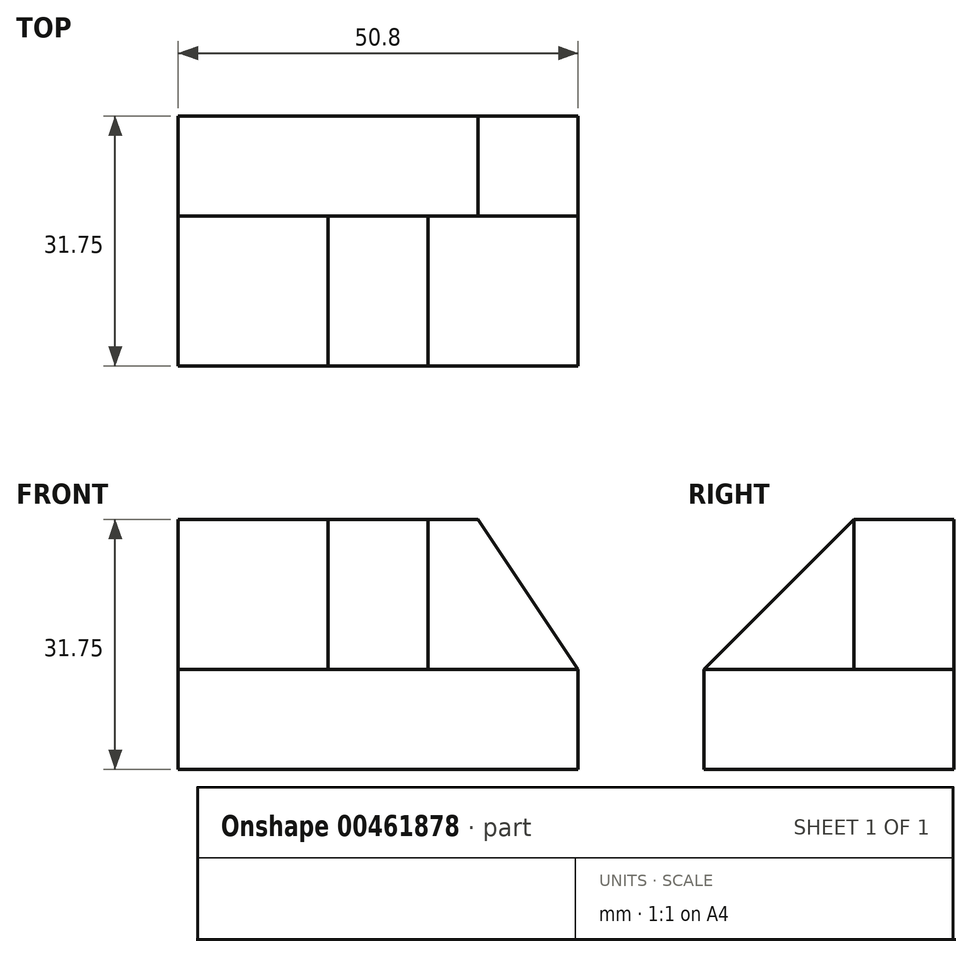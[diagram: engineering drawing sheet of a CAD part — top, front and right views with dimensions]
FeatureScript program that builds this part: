
annotation { "Feature Type Name" : "Feature", "Feature Type Description" : "" }
export const myFeature = defineFeature(function(context is Context, id is Id, definition is map)
    precondition{}
    {
        {
            var Q0;
            Q0=qCreatedBy(makeId("Right.planeOp"),FACE);
            var sketch = newSketch(context, id + "F0", { "sketchPlane" : qUnion([Q0])});
            skLineSegment(sketch, "E0.bottom", {"start": v(0, 0) * mm, "end": v(31.75, 0) * mm});
            skLineSegment(sketch, "E0.top", {"start": v(0, 31.75) * mm, "end": v(31.75, 31.75) * mm});
            skLineSegment(sketch, "E0.left", {"start": v(0, 0) * mm, "end": v(0, 31.75) * mm});
            skLineSegment(sketch, "E0.right", {"start": v(31.75, 0) * mm, "end": v(31.75, 31.75) * mm});
            skSolve(sketch);
        }
        {
            var Q0;
            Q0 = qSketchRegion(id + "F0", true);
            extrude(context, id + "F1", {"entities" : qUnion([Q0]), "depth" : 50.8 * mm});
        }
        {
            var Q0;
            Q0=makeQuery(id+"F1.opExtrude","CAP_FACE",FACE,{"disambiguationData":[OSD([sQuery(id+"F0.wireOp",EDGE,"E0.bottom"),sQuery(id+"F0.wireOp",EDGE,"E0.top"),sQuery(id+"F0.wireOp",EDGE,"E0.left"),sQuery(id+"F0.wireOp",EDGE,"E0.right")])],"isStart":false});
            var sketch = newSketch(context, id + "F2", { "sketchPlane" : qUnion([Q0])});
            skLineSegment(sketch, "E1", {"start": v(31.75, 31.75) * mm, "end": v(19.05, 31.75) * mm});
            skLineSegment(sketch, "E2", {"start": v(19.05, 31.75) * mm, "end": v(19.05, 12.7) * mm});
            skLineSegment(sketch, "E3", {"start": v(19.05, 12.7) * mm, "end": v(0, 12.7) * mm});
            skLineSegment(sketch, "E4", {"start": v(0, 12.7) * mm, "end": v(0, 0) * mm});
            skLineSegment(sketch, "E5", {"start": v(0, 12.7) * mm, "end": v(19.05, 31.75) * mm});
            skSolve(sketch);
        }
        {
            var Q0;
            {var subQ0=sQuery(id+"F2.wireOp",EDGE,"E5");Q0=makeQuery(id+"F2.imprint","IMPRINT",FACE,{"disambiguationData":[TD([[makeQuery(id+"F2.imprint","IMPRINT",EDGE,{"derivedFrom":subQ0}),1.0]])]});}
            extrude(context, id + "F3", {"entities" : qUnion([Q0]), "operationType" : NewBodyOperationType.REMOVE, "oppositeDirection" : true, "depth" : 50.8 * mm});
        }
        {
            var Q0;
            Q0=makeQuery(id+"F1.opExtrude","CAP_FACE",FACE,{"disambiguationData":[OSD([sQuery(id+"F0.wireOp",EDGE,"E0.bottom"),sQuery(id+"F0.wireOp",EDGE,"E0.top"),sQuery(id+"F0.wireOp",EDGE,"E0.left"),sQuery(id+"F0.wireOp",EDGE,"E0.right")])],"isStart":false});
            var sketch = newSketch(context, id + "F4", { "sketchPlane" : qUnion([Q0])});
            skLineSegment(sketch, "E6", {"start": v(19.05, 31.75) * mm, "end": v(0, 12.7) * mm});
            skLineSegment(sketch, "E7", {"start": v(0, 12.7) * mm, "end": v(19.05, 12.7) * mm});
            skLineSegment(sketch, "E8", {"start": v(19.05, 12.7) * mm, "end": v(19.05, 31.75) * mm});
            skSolve(sketch);
        }
        {
            var Q0;
            Q0=makeQuery(id+"F4.imprint","IMPRINT",FACE,{"disambiguationData":[TD([[makeQuery(id+"F4.imprint","IMPRINT",EDGE,{"derivedFrom":sQuery(id+"F4.wireOp",EDGE,"E6")}),-1.0]])]});
            extrude(context, id + "F5", {"entities" : qUnion([Q0]), "operationType" : NewBodyOperationType.REMOVE, "oppositeDirection" : true, "depth" : 19.05 * mm});
        }
        {
            var Q0;
            Q0=makeQuery(id+"F5.boolean.opBoolean","COPY",FACE,{"derivedFrom":makeQuery(id+"F5.opExtrude","SWEPT_FACE",FACE,{"disambiguationData":[OSD([sQuery(id+"F4.wireOp",EDGE,"E8")])]})});
            var sketch = newSketch(context, id + "F6", { "sketchPlane" : qUnion([Q0])});
            skLineSegment(sketch, "E9", {"start": v(50.8, 31.75) * mm, "end": v(38.07, 31.75) * mm});
            skLineSegment(sketch, "E10", {"start": v(38.07, 31.75) * mm, "end": v(50.8, 12.7) * mm});
            skSolve(sketch);
        }
        {
            var Q0;
            Q0=makeQuery(id+"F6.imprint","IMPRINT",FACE,{"disambiguationData":[TD([[makeQuery(id+"F6.imprint","IMPRINT",EDGE,{"derivedFrom":sQuery(id+"F6.wireOp",EDGE,"E9")}),-1.0]])]});
            extrude(context, id + "F7", {"entities" : qUnion([Q0]), "operationType" : NewBodyOperationType.REMOVE, "oppositeDirection" : true, "depth" : 12.7 * mm});
        }
        {
            var Q0;
            Q0=makeQuery(id+"F1.opExtrude","CAP_FACE",FACE,{"disambiguationData":[OSD([sQuery(id+"F0.wireOp",EDGE,"E0.bottom"),sQuery(id+"F0.wireOp",EDGE,"E0.top"),sQuery(id+"F0.wireOp",EDGE,"E0.left"),sQuery(id+"F0.wireOp",EDGE,"E0.right")])],"isStart":true});
            var sketch = newSketch(context, id + "F8", { "sketchPlane" : qUnion([Q0])});
            skLineSegment(sketch, "E11", {"start": v(-19.05, 31.75) * mm, "end": v(0, 12.7) * mm});
            skLineSegment(sketch, "E12", {"start": v(0, 12.7) * mm, "end": v(-19.05, 12.7) * mm});
            skLineSegment(sketch, "E13", {"start": v(-19.05, 12.7) * mm, "end": v(-19.05, 31.75) * mm});
            skSolve(sketch);
        }
        {
            var Q0;
            Q0=makeQuery(id+"F8.imprint","IMPRINT",FACE,{"disambiguationData":[TD([[makeQuery(id+"F8.imprint","IMPRINT",EDGE,{"derivedFrom":sQuery(id+"F8.wireOp",EDGE,"E11")}),1.0]])]});
            extrude(context, id + "F9", {"entities" : qUnion([Q0]), "operationType" : NewBodyOperationType.REMOVE, "oppositeDirection" : true, "depth" : 19.05 * mm});
        }
    });
